# Revit family: Domotics-DomesticRanges-GEWISS-SYSTEM_COMMAND-INTERMEDIATE_SWITCH_2M
name_source: partatom
category: Apparecchi elettrici
revit_build: Autodesk Revit 2016 (Build: 20161004_0715(x64)
units: mm (PartAtom-declared; Revit-internal decimal feet)

## family parameters
Condiviso = Sì
Host = Superficie
Mantenere orientamento annotazione = Sì
Numero OmniClass = 23.80.50.11.14
Punto di calcolo locali = Sì
Quota connettore circolare = Usa diametro
Taglio con vuoti quando caricato = No
Tipo di parte = Normale
Titolo OmniClass = Switches

## types (2) — shared parameters
Button key = With diffuser
Catalogue = DOMOTICS
Catalogue Range = SYSTEM - DOMESTIC RANGE
Description. = Intermediate switch
Description: = 1P - 16 AX - illuminable
Electrocod = 0130
IDF = f87f264a-01c4-42e4-a64f-612872003f8b
IDT = 27985029-19b1-431e-9c8f-25b93fdf3787
Immagine tipo = GW21580.jpg
Larghezza pulsante = 46 mm  [stored 0.150919 ft]
No. SYSTEM modules = 2
Produttore = GEWISS S.p.A.
Prospetto di default = 1219 mm
SEO = Intermediate switch
Simbolo_ = SIMBOLO INVERTITORI : INV1PLUM
Technical sheet = https://www.gewiss.com
Tipo_ = SYSTEM INVERTITORI 2M_BASE : NERO
Type = Intermediate switch
URL = https://www.gewiss.com
Version file RFA = 19.4
Voltage = 250 V ac
Voltage: = 250 V ac

## per-type parameters (varying)
| type | Colour | Descrizione | EAN code | Modello |
| GW21580 - Rev.-switch-illuminable 16Ax 2M black | Black | REV.-SWITCH-ILLUMINABLE 16AX 2M SY/BK | 8011564184398 | GW21580 |
| GW20580 - Rev.-switch-illuminable 16Ax 2M white | White | REV.-SWITCH-ILLUMINABLE 16AX 2M SY/WT | 8011564184381 | GW20580 |

note: [stored X ft] marks values corroborated as IEEE doubles in the binary element streams (Revit-internal decimal feet)

## geometry (parser evidence)
native form markers: Sweep x2
no freeform markers — native parametric forms only
